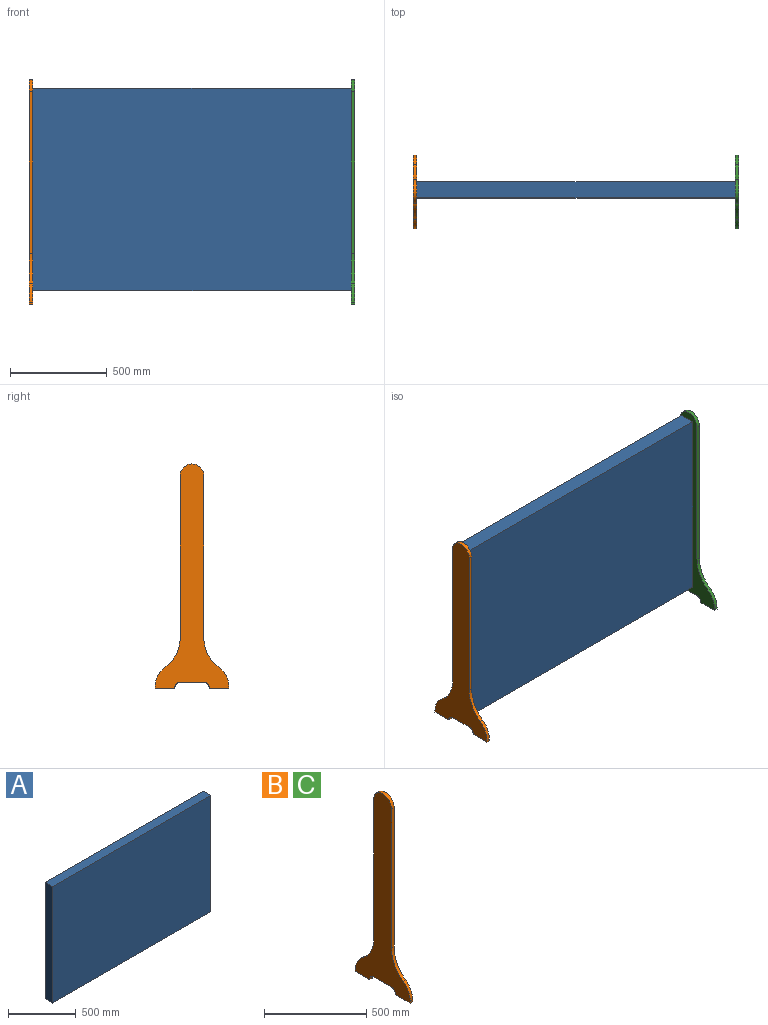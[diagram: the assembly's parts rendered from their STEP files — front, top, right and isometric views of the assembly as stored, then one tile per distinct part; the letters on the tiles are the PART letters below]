
ASSEMBLY  parts=3 mates=4
PART A: 6 faces, bbox 1650x82x1050 mm
  f0: plane 1650x82mm, normal (0,0,1), area 135300mm2, adj f1,f3,f4,f5
  f1: plane 1050x82mm, normal (-1,0,0), area 86100mm2, adj f0,f2,f4,f5
  f2: plane 1650x82mm, normal (0,0,-1), area 135300mm2, adj f1,f3,f4,f5
  f3: plane 1050x82mm, normal (1,0,0), area 86100mm2, adj f0,f2,f4,f5
  f4: plane 1650x1050mm, normal (0,-1,0), area 1732500mm2, adj f0,f1,f2,f3
  f5: plane 1650x1050mm, normal (0,1,0), area 1732500mm2, adj f0,f1,f2,f3
PART B: 16 faces, bbox 18x380x1161 mm
  f0: plane 837.47x18mm, normal (0,1,0), area 15074.5mm2, adj f1,f13,f14,f15
  f1: cylinder r=61mm len=122mm, axis (-1,0,0), area 3449.5mm2, adj f0,f2,f14,f15
  f2: plane 837.47x18mm, normal (0,-1,0), area 15074.5mm2, adj f1,f3,f14,f15
  f3: cylinder r=193.47mm len=156.76mm, axis (-1,0,0), area 3289.5mm2, adj f2,f4,f14,f15
  f4: cylinder r=118.19mm len=95.76mm, axis (-1,0,0), area 2009.5mm2, adj f3,f5,f14,f15
  f5: plane 18x10mm, normal (0,-1,0), area 180mm2, adj f4,f6,f14,f15
  f6: plane 100x18mm, normal (0,0,-1), area 1800mm2, adj f5,f7,f14,f15
  f7: cylinder r=30mm len=30mm, axis (-1,0,0), area 848.2mm2, adj f6,f8,f14,f15
  f8: plane 120x18mm, normal (0,0,-1), area 2160mm2, adj f7,f9,f14,f15
  f9: cylinder r=30mm len=30mm, axis (-1,0,0), area 848.2mm2, adj f8,f10,f14,f15
  f10: plane 100x18mm, normal (0,0,-1), area 1800mm2, adj f9,f11,f14,f15
  f11: plane 18x10mm, normal (0,1,0), area 180mm2, adj f10,f12,f14,f15
  f12: cylinder r=118.19mm len=95.76mm, axis (-1,0,0), area 2009.5mm2, adj f11,f13,f14,f15
  f13: cylinder r=193.47mm len=156.76mm, axis (-1,0,0), area 3289.5mm2, adj f0,f12,f14,f15
  f14: plane 1161x380mm, normal (1,0,0), area 167035.5mm2, adj f0,f1,f2,f3,f4,f5,f6,f7
  f15: plane 1161x380mm, normal (-1,0,0), area 167035.5mm2, adj f0,f1,f2,f3,f4,f5,f6,f7
PART C: same geometry as B
PLACE A t=(9.12,-30,192.8)mm
PLACE B t=(-833.88,-80.51,174.32)mm
PLACE C t=(834.12,-80.51,174.32)mm
MATE planar C.f15 <-> A.f3  axis (-1,0,0) through (834.12,-80.51,93.87)mm
MATE planar B.f6 <-> C.f6  axis (0,0,-1) through (-824.88,-170.51,-400.68)mm
MATE planar B.f2 <-> C.f2  axis (0,-1,0) through (-824.88,-141.51,280.59)mm
MATE planar A.f1 <-> B.f14  axis (-1,0,0) through (-815.88,-71,192.8)mm
